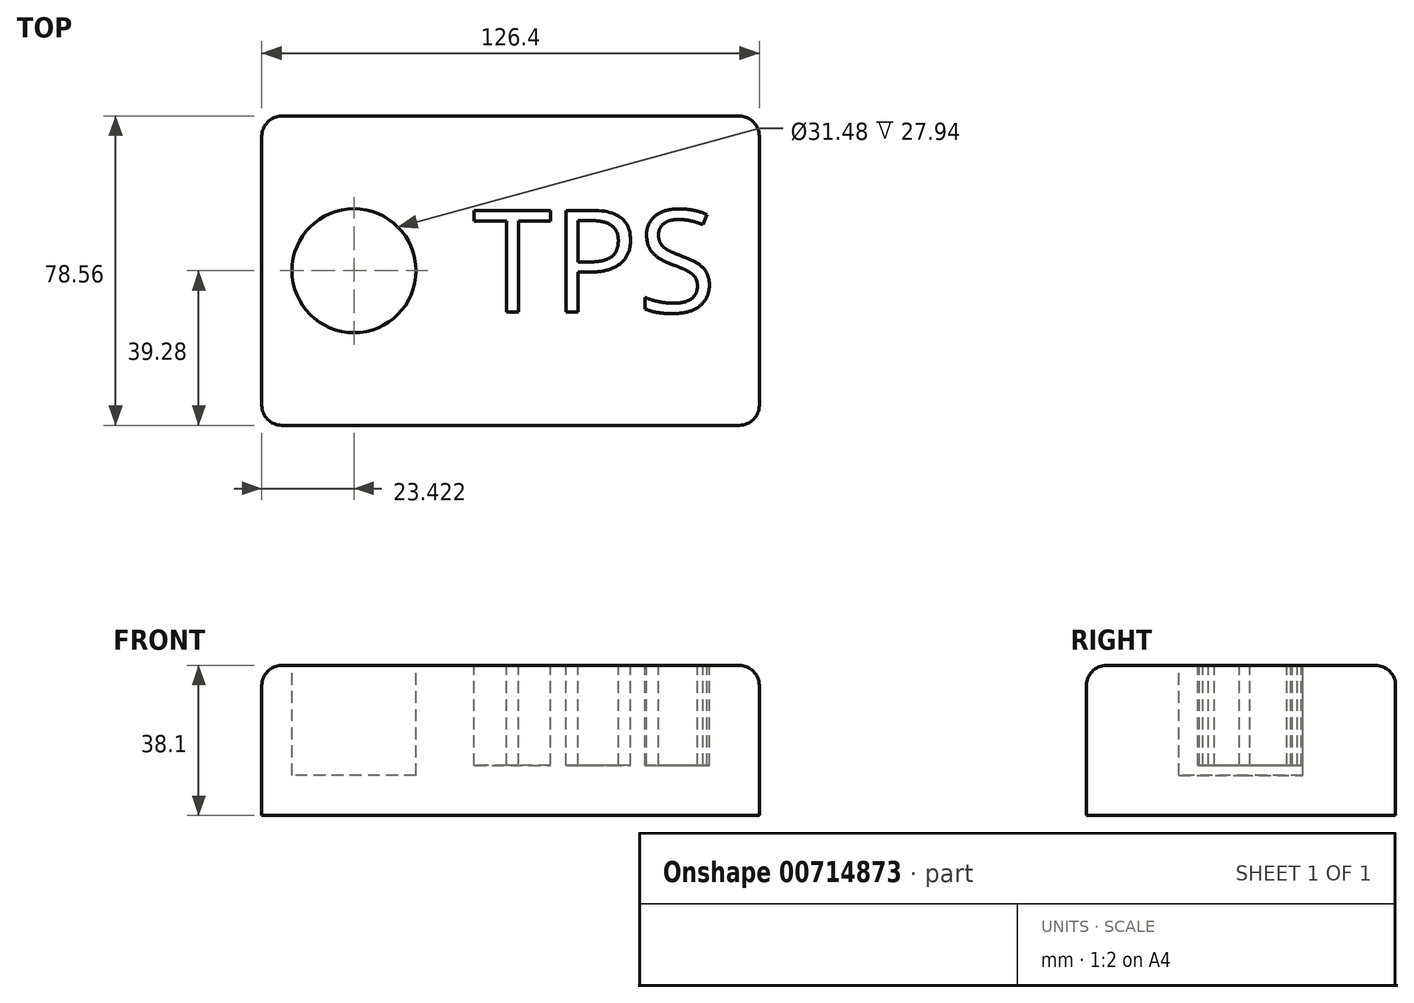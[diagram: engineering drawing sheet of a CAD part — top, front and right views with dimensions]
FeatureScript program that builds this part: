
annotation { "Feature Type Name" : "Feature", "Feature Type Description" : "" }
export const myFeature = defineFeature(function(context is Context, id is Id, definition is map)
    precondition{}
    {
        {
            var Q0;
            Q0=qCreatedBy(makeId("Top.planeOp"),FACE);
            var sketch = newSketch(context, id + "F0", { "sketchPlane" : qUnion([Q0])});
            skLineSegment(sketch, "E0.bottom", {"start": v(10.33, -39.28) * mm, "end": v(-116.07, -39.28) * mm});
            skLineSegment(sketch, "E0.top", {"start": v(10.33, 39.28) * mm, "end": v(-116.07, 39.28) * mm});
            skLineSegment(sketch, "E0.left", {"start": v(10.33, -39.28) * mm, "end": v(10.33, 39.28) * mm});
            skLineSegment(sketch, "E0.right", {"start": v(-116.07, -39.28) * mm, "end": v(-116.07, 39.28) * mm});
            skPoint(sketch, "E0.middle", {"position": v(-52.87, 0) * mm});
            skSolve(sketch);
        }
        {
            var Q0;
            Q0=makeQuery(id+"F0.imprint","IMPRINT",FACE,{"disambiguationData":[TD([[makeQuery(id+"F0.imprint","IMPRINT",EDGE,{"derivedFrom":sQuery(id+"F0.wireOp",EDGE,"E0.bottom")}),-1.0]])]});
            extrude(context, id + "F1", {"entities" : qUnion([Q0]), "depth" : 38.1 * mm, "offsetDistance" : 25.4 * mm});
        }
        {
            var Q0;
            Q0=makeQuery(id+"F1.opExtrude","CAP_FACE",FACE,{"disambiguationData":[OSD([sQuery(id+"F0.wireOp",EDGE,"E0.bottom"),sQuery(id+"F0.wireOp",EDGE,"E0.top"),sQuery(id+"F0.wireOp",EDGE,"E0.left"),sQuery(id+"F0.wireOp",EDGE,"E0.right")])],"isStart":false});
            var sketch = newSketch(context, id + "F2", { "sketchPlane" : qUnion([Q0])});
            skText(sketch, "E1", { "text": "TPS", "fontName": "OpenSans-Regular.ttf"});
            const initialGuessF2  = {"E1": [-0.06242, -0.01054, 1, 0, 0.02611]};
            skSetInitialGuess(sketch, initialGuessF2);
            skSolve(sketch);
        }
        {
            var Q0;
            Q0 = qSketchRegion(id + "F2", true);
            extrude(context, id + "F3", {"entities" : qUnion([Q0]), "operationType" : NewBodyOperationType.REMOVE, "oppositeDirection" : true, "depth" : 25.4 * mm, "offsetDistance" : 25.4 * mm});
        }
        {
            var Q0;
            Q0=makeQuery(id+"F1.opExtrude","CAP_EDGE",EDGE,{"disambiguationData":[OSD([sQuery(id+"F0.wireOp",EDGE,"E0.right")])],"isStart":false});
            fillet(context, id + "F4", {"entities" : qUnion([Q0]), "radius" : 5.08 * mm, "tangentPropagation" : true, "allowEdgeOverflow" : false});
        }
        {
            var Q0;
            Q0=makeQuery(id+"F1.opExtrude","CAP_EDGE",EDGE,{"disambiguationData":[OSD([sQuery(id+"F0.wireOp",EDGE,"E0.bottom")])],"isStart":false});
            fillet(context, id + "F5", {"entities" : qUnion([Q0]), "radius" : 5.08 * mm, "tangentPropagation" : true, "allowEdgeOverflow" : false});
        }
        {
            var Q0;
            Q0=makeQuery(id+"F1.opExtrude","CAP_EDGE",EDGE,{"disambiguationData":[OSD([sQuery(id+"F0.wireOp",EDGE,"E0.left")])],"isStart":false});
            fillet(context, id + "F6", {"entities" : qUnion([Q0]), "radius" : 5.08 * mm, "tangentPropagation" : true, "allowEdgeOverflow" : false});
        }
        {
            var Q0;
            Q0=makeQuery(id+"F1.opExtrude","CAP_EDGE",EDGE,{"disambiguationData":[OSD([sQuery(id+"F0.wireOp",EDGE,"E0.top")])],"isStart":false});
            fillet(context, id + "F7", {"entities" : qUnion([Q0]), "radius" : 5.08 * mm, "tangentPropagation" : true, "allowEdgeOverflow" : false});
        }
        {
            var Q0;
            {var subQ0=sQuery(id+"F0.wireOp",EDGE,"E0.top");var subQ1=sQuery(id+"F0.wireOp",EDGE,"E0.right");var subQ2=sQuery(id+"F0.wireOp",EDGE,"E0.bottom");var subQ3=sQuery(id+"F0.wireOp",EDGE,"E0.left");Q0=makeQuery(id+"F3.boolean.opBoolean","SPLIT",FACE,{"disambiguationData":[TD([makeQuery(id+"F1.opExtrude","SWEPT_FACE",FACE,{"disambiguationData":[OSD([subQ2])]})])],"derivedFrom":makeQuery(id+"F1.opExtrude","CAP_FACE",FACE,{"disambiguationData":[OSD([subQ2,subQ0,subQ3,subQ1])],"isStart":false})});}
            var sketch = newSketch(context, id + "F8", { "sketchPlane" : qUnion([Q0])});
            skCircle(sketch, "E2", {"center": v(-92.65, 0) * mm, "radius": 15.74 * mm});
            skPoint(sketch, "E2.centerSnap0", {"position": v(-110.99, 0) * mm});
            skSolve(sketch);
        }
        {
            var Q0;
            Q0 = qSketchRegion(id + "F8", true);
            extrude(context, id + "F9", {"entities" : qUnion([Q0]), "operationType" : NewBodyOperationType.REMOVE, "oppositeDirection" : true, "depth" : 27.94 * mm, "offsetDistance" : 25.4 * mm});
        }
    });
